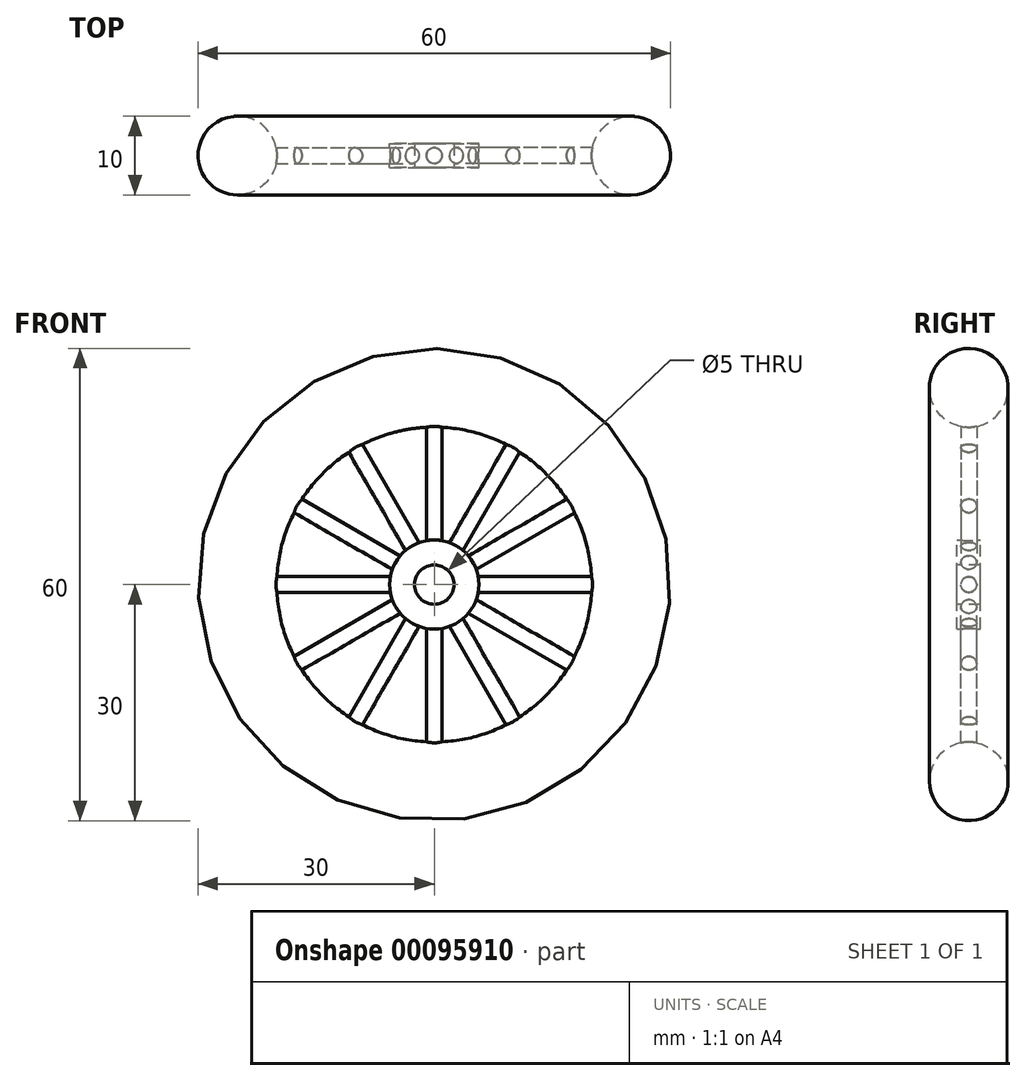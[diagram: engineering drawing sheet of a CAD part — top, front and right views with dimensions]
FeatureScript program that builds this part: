
annotation { "Feature Type Name" : "Feature", "Feature Type Description" : "" }
export const myFeature = defineFeature(function(context is Context, id is Id, definition is map)
    precondition{}
    {
        {
            var Q0;
            Q0=qCreatedBy(makeId("Right.planeOp"),FACE);
            var sketch = newSketch(context, id + "F0", { "sketchPlane" : qUnion([Q0])});
            skLineSegment(sketch, "E0", {"start": v(0, 0) * mm, "end": v(-121.49, 0) * mm, "construction": true});
            skCircle(sketch, "E1", {"center": v(0, 25) * mm, "radius": 5 * mm});
            skSolve(sketch);
        }
        {
            var Q0;
            Q0 = qSketchRegion(id + "F0", true);
            var Q1;
            Q1=sQuery(id+"F0.wireOp",EDGE,"E0");
            revolve(context, id + "F1", {"entities" : qUnion([Q0]), "axis" : qUnion([Q1]), "revolveType" : RevolveType.FULL});
        }
        {
            var Q0;
            Q0=qCreatedBy(makeId("Front.planeOp"),FACE);
            var sketch = newSketch(context, id + "F2", { "sketchPlane" : qUnion([Q0])});
            skCircle(sketch, "E2", {"center": v(0, 0) * mm, "radius": 5.66 * mm});
            skSolve(sketch);
        }
        {
            var Q0;
            Q0 = qSketchRegion(id + "F2", true);
            extrude(context, id + "F3", {"entities" : qUnion([Q0]), "endBound" : BoundingType.SYMMETRIC, "depth" : 3 * mm});
        }
        {
            var Q0;
            Q0=qCreatedBy(makeId("Right.planeOp"),FACE);
            var sketch = newSketch(context, id + "F4", { "sketchPlane" : qUnion([Q0])});
            skCircle(sketch, "E3", {"center": v(0, 0) * mm, "radius": 1 * mm});
            skSolve(sketch);
        }
        {
            var Q0;
            Q0 = qSketchRegion(id + "F4", true);
            extrude(context, id + "F5", {"entities" : qUnion([Q0]), "operationType" : NewBodyOperationType.ADD, "depth" : 25 * mm});
        }
        {
            var Q0;
            Q0=makeQuery(id+"F1.opRevolve","SWEPT_BODY",BODY,{"disambiguationData":[OSD([sQuery(id+"F0.wireOp",EDGE,"E1")])]});
            var Q1;
            Q1=sQuery(id+"F0.wireOp",EDGE,"E0");
            circularPattern(context, id + "F6", {"operationType" : NewBodyOperationType.ADD, "entities" : qUnion([Q0]), "axis" : qUnion([Q1]), "angle" : 30 * degree, "instanceCount" : 12});
        }
        {
            var Q0;
            Q0=makeQuery(id+"F3.opExtrude","CAP_FACE",FACE,{"disambiguationData":[OSD([sQuery(id+"F2.wireOp",EDGE,"E2")])],"isStart":false});
            var sketch = newSketch(context, id + "F7", { "sketchPlane" : qUnion([Q0])});
            skCircle(sketch, "E4", {"center": v(0, 0) * mm, "radius": 2.5 * mm});
            skSolve(sketch);
        }
        {
            var Q0;
            Q0 = qSketchRegion(id + "F7", true);
            extrude(context, id + "F8", {"entities" : qUnion([Q0]), "operationType" : NewBodyOperationType.REMOVE, "endBound" : BoundingType.THROUGH_ALL, "oppositeDirection" : true, "depth" : 25 * mm});
        }
    });
